# Revit family: Casement_30.5_A_Top_Hung_Standard
name_source: partatom
category: Windows
revit_build: Autodesk Revit 2014 (Build: 20130308_1515(x64)
units: mm (PartAtom-declared; Revit-internal decimal feet)

## types (6) — shared parameters
Aluminium Thickness = 1 mm  [stored 0.00328084 ft]
Bead SG Gap = 13 mm  [stored 0.0426509 ft]
Bottom Hung = No
Casement Dimension = 31 mm  [stored 0.101706 ft]
Custom Window Height = 590 mm  [stored 1.9357 ft]
DG Extrusion Start = 5 mm  [stored 0.0164042 ft]
DG Gasket Finish = Double Glazing Gasket Material
DG Thickness = 3 mm  [stored 0.00984252 ft]
DG Thickness Calc = 3 mm  [stored 0.00984252 ft]
Default Sill Height = 800 mm  [stored 2.62467 ft]
Depth Bead = 17 mm
Description = Window 30.5mm, Type A top hung
Double Glazing = No
Frame Center Offset = 15 mm  [stored 0.0492126 ft]
Height = 590 mm  [stored 1.9357 ft]
Height Sash = 514 mm
Height Sash 1 Opening = 545 mm  [stored 1.78806 ft]
Limit Sash Height Max = 750 mm  [stored 2.46063 ft]
Limit Sash Height Min = 300 mm  [stored 0.984252 ft]
Limit Sash Width Max = 1000 mm  [stored 3.28084 ft]
Limit Sash Width Min = 300 mm  [stored 0.984252 ft]
Limit Window Height Max = 796 mm  [stored 2.61155 ft]
Limit Window Height Min = 346 mm
Limit Window Width Max = 1046 mm  [stored 3.43176 ft]
Limit Window Width Min = 346 mm
Manufacturer = Crealco
Max System DG One Piece Thickness = 3 mm  [stored 0.00984252 ft]
Max System DG Unit Thickness = 18 mm  [stored 0.0590551 ft]
Model = Casement 30.5
Offset Bead SG Center Reversed = 15 mm  [stored 0.0492126 ft]
Offset Sash 1 Top = 23 mm  [stored 0.0754593 ft]
Offset Sash Left = 23 mm  [stored 0.0754593 ft]
Offset Window Exterior = 15 mm  [stored 0.0492126 ft]
SG Gasket Thickness = 6 mm  [stored 0.019685 ft]
Sash Center Offset = 12 mm  [stored 0.0393701 ft]
Sash Height = 545 mm  [stored 1.78806 ft]
Sash Overlap = 7 mm  [stored 0.0229659 ft]
Sash Spacing Inner = 8 mm  [stored 0.0262467 ft]
Top Hung = Yes
URL = http://www.crealco.co.za
Wall Closure = By host
Width Bead = 15 mm  [stored 0.0492126 ft]
Width Profile = 30 mm  [stored 0.0984252 ft]
zero-valued in all types: Window Exterior Offset

## per-type parameters (varying)
| type | Clearvue SHGC Value | Clearvue U Value | Custom Windload | Custom Window Width | Energy Advantage SHGC Value | Intruderprufe LowE SHGC Value | Intruderprufe LowE U Value | Intruderprufe SHGC Value | Intruderprufe U Value | Max Pane Area | Sash Width | Width | Width Sash | Width Sash Opening | Windload Design |
| 305-0606T-1000Pa | 0.503 | 6.18 | 1000 mm  [stored 3.28084 ft] | 590 mm  [stored 1.9357 ft] | 0.452 | 0.426 | 4.92 | 0.477 | 6.05 | 0.2 m² | 545 mm  [stored 1.78806 ft] | 590 mm  [stored 1.9357 ft] | 514 mm | 545 mm  [stored 1.78806 ft] | 1000 mm  [stored 3.28084 ft] |
| 305-0906T-1000Pa | 0.553 | 6.14 | 1000 mm  [stored 3.28084 ft] | 890 mm  [stored 2.91995 ft] | 0.496 | 0.466 | 4.73 | 0.524 | 6 | 0.33 m² | 845 mm  [stored 2.77231 ft] | 890 mm  [stored 2.91995 ft] | 814 mm  [stored 2.6706 ft] | 845 mm  [stored 2.77231 ft] | 1000 mm  [stored 3.28084 ft] |
| 305-0606T-1500Pa | 0.503 | 6.18 | 1500 mm  [stored 4.92126 ft] | 590 mm  [stored 1.9357 ft] | 0.452 | 0.426 | 4.92 | 0.477 | 6.05 | 0.2 m² | 545 mm  [stored 1.78806 ft] | 590 mm  [stored 1.9357 ft] | 514 mm | 545 mm  [stored 1.78806 ft] | 1500 mm  [stored 4.92126 ft] |
| 305-0606T-2000Pa | 0.503 | 6.18 | 2000 mm  [stored 6.56168 ft] | 590 mm  [stored 1.9357 ft] | 0.452 | 0.426 | 4.92 | 0.477 | 6.05 | 0.2 m² | 545 mm  [stored 1.78806 ft] | 590 mm  [stored 1.9357 ft] | 514 mm | 545 mm  [stored 1.78806 ft] | 2000 mm  [stored 6.56168 ft] |
| 305-0906T-1500Pa | 0.553 | 6.14 | 1500 mm  [stored 4.92126 ft] | 890 mm  [stored 2.91995 ft] | 0.496 | 0.466 | 4.73 | 0.524 | 6 | 0.33 m² | 845 mm  [stored 2.77231 ft] | 890 mm  [stored 2.91995 ft] | 814 mm  [stored 2.6706 ft] | 845 mm  [stored 2.77231 ft] | 1500 mm  [stored 4.92126 ft] |
| 305-0906T-2000Pa | 0.553 | 6.14 | 2000 mm  [stored 6.56168 ft] | 890 mm  [stored 2.91995 ft] | 0.496 | 0.466 | 4.73 | 0.524 | 6 | 0.33 m² | 845 mm  [stored 2.77231 ft] | 890 mm  [stored 2.91995 ft] | 814 mm  [stored 2.6706 ft] | 845 mm  [stored 2.77231 ft] | 2000 mm  [stored 6.56168 ft] |

note: [stored X ft] marks values corroborated as IEEE doubles in the binary element streams (Revit-internal decimal feet)

## geometry (parser evidence)
native form markers: Sweep x31
no freeform markers — native parametric forms only
